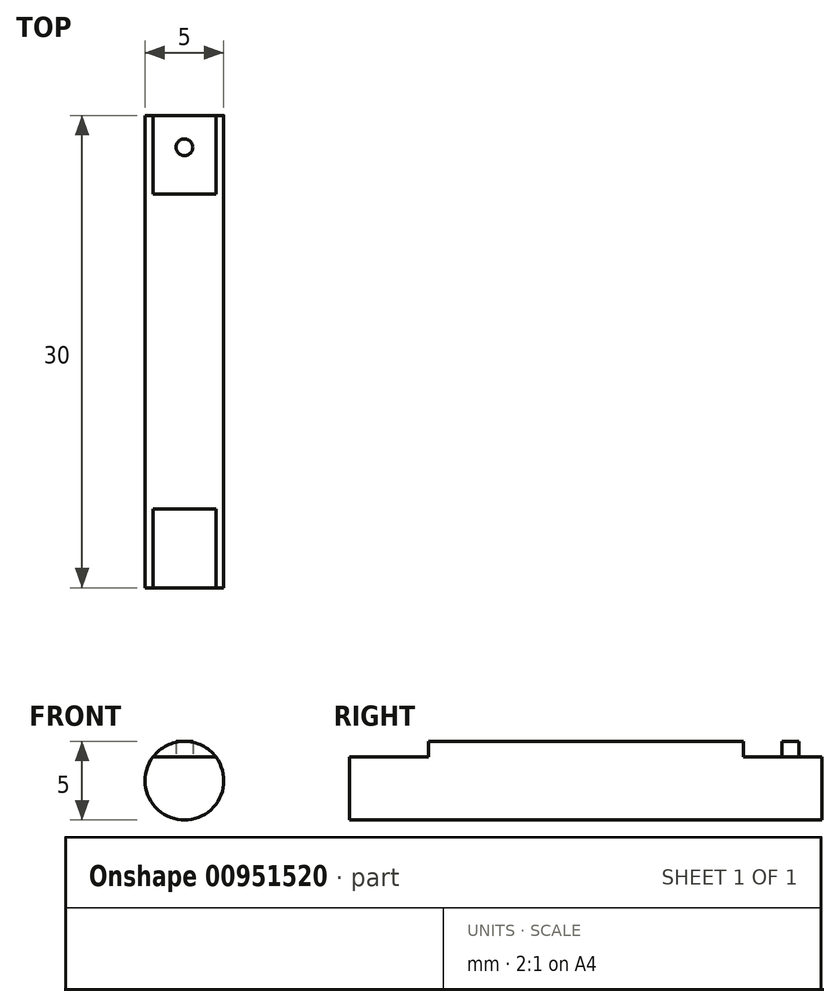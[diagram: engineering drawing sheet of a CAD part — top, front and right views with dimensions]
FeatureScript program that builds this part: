
annotation { "Feature Type Name" : "Feature", "Feature Type Description" : "" }
export const myFeature = defineFeature(function(context is Context, id is Id, definition is map)
    precondition{}
    {
        {
            var Q0;
            Q0=qCreatedBy(makeId("Front.planeOp"),FACE);
            var sketch = newSketch(context, id + "F0", { "sketchPlane" : qUnion([Q0])});
            skCircle(sketch, "E0", {"center": v(0, 0) * mm, "radius": 2.5 * mm});
            skLineSegment(sketch, "E1", {"start": v(-2, 1.5) * mm, "end": v(2, 1.5) * mm});
            skSolve(sketch);
        }
        {
            var Q0;
            {var subQ0=sQuery(id+"F0.wireOp",EDGE,"E1");Q0=makeQuery(id+"F0.imprint","IMPRINT",FACE,{"disambiguationData":[TD([[makeQuery(id+"F0.imprint","IMPRINT",EDGE,{"derivedFrom":subQ0}),-1.0]])]});}
            extrude(context, id + "F1", {"entities" : qUnion([Q0]), "depth" : 30 * mm, "offsetDistance" : 25 * mm});
        }
        {
            var Q0;
            Q0=makeQuery(id+"F1.opExtrude","CAP_FACE",FACE,{"disambiguationData":[OSD([sQuery(id+"F0.wireOp",EDGE,"E0"),sQuery(id+"F0.wireOp",EDGE,"E1")])],"isStart":false});
            var sketch = newSketch(context, id + "F2", { "sketchPlane" : qUnion([Q0])});
            skCircle(sketch, "E2", {"center": v(0, 0) * mm, "radius": 2.5 * mm});
            skSolve(sketch);
        }
        {
            var Q0;
            Q0=qSketchRegion(id+"F2",true);
            extrude(context, id + "F3", {"entities" : qUnion([Q0]), "operationType" : NewBodyOperationType.ADD, "oppositeDirection" : true, "depth" : 25 * mm, "offsetDistance" : 25 * mm, "hasSecondDirection" : true, "secondDirectionOppositeDirection" : true, "secondDirectionDepth" : 5 * mm});
        }
        {
            var Q0;
            {var subQ1=sQuery(id+"F0.wireOp",EDGE,"E1");var subQ2=sQuery(id+"F2.wireOp",EDGE,"E2");Q0=makeQuery(id+"F3.boolean.opBoolean","SPLIT",FACE,{"disambiguationData":[TD([makeQuery(id+"F3.opExtrude","CAP_FACE",FACE,{"disambiguationData":[OSD([subQ2])],"isStart":true})])],"derivedFrom":makeQuery(id+"F1.opExtrude","SWEPT_FACE",FACE,{"disambiguationData":[OSD([subQ1])]})});}
            var sketch = newSketch(context, id + "F4", { "sketchPlane" : qUnion([Q0])});
            skCircle(sketch, "E3", {"center": v(0, -2.02) * mm, "radius": 0.53 * mm});
            skSolve(sketch);
        }
        {
            var Q0;
            Q0 = qSketchRegion(id + "F4", true);
            extrude(context, id + "F5", {"entities" : qUnion([Q0]), "operationType" : NewBodyOperationType.ADD, "depth" : 1 * mm, "offsetDistance" : 25 * mm});
        }
        {
            var Q0;
            Q0 = qSketchRegion(id + "F4", true);
            extrude(context, id + "F6", {"entities" : qUnion([Q0]), "operationType" : NewBodyOperationType.ADD, "depth" : 1 * mm, "offsetDistance" : 25 * mm});
        }
    });
